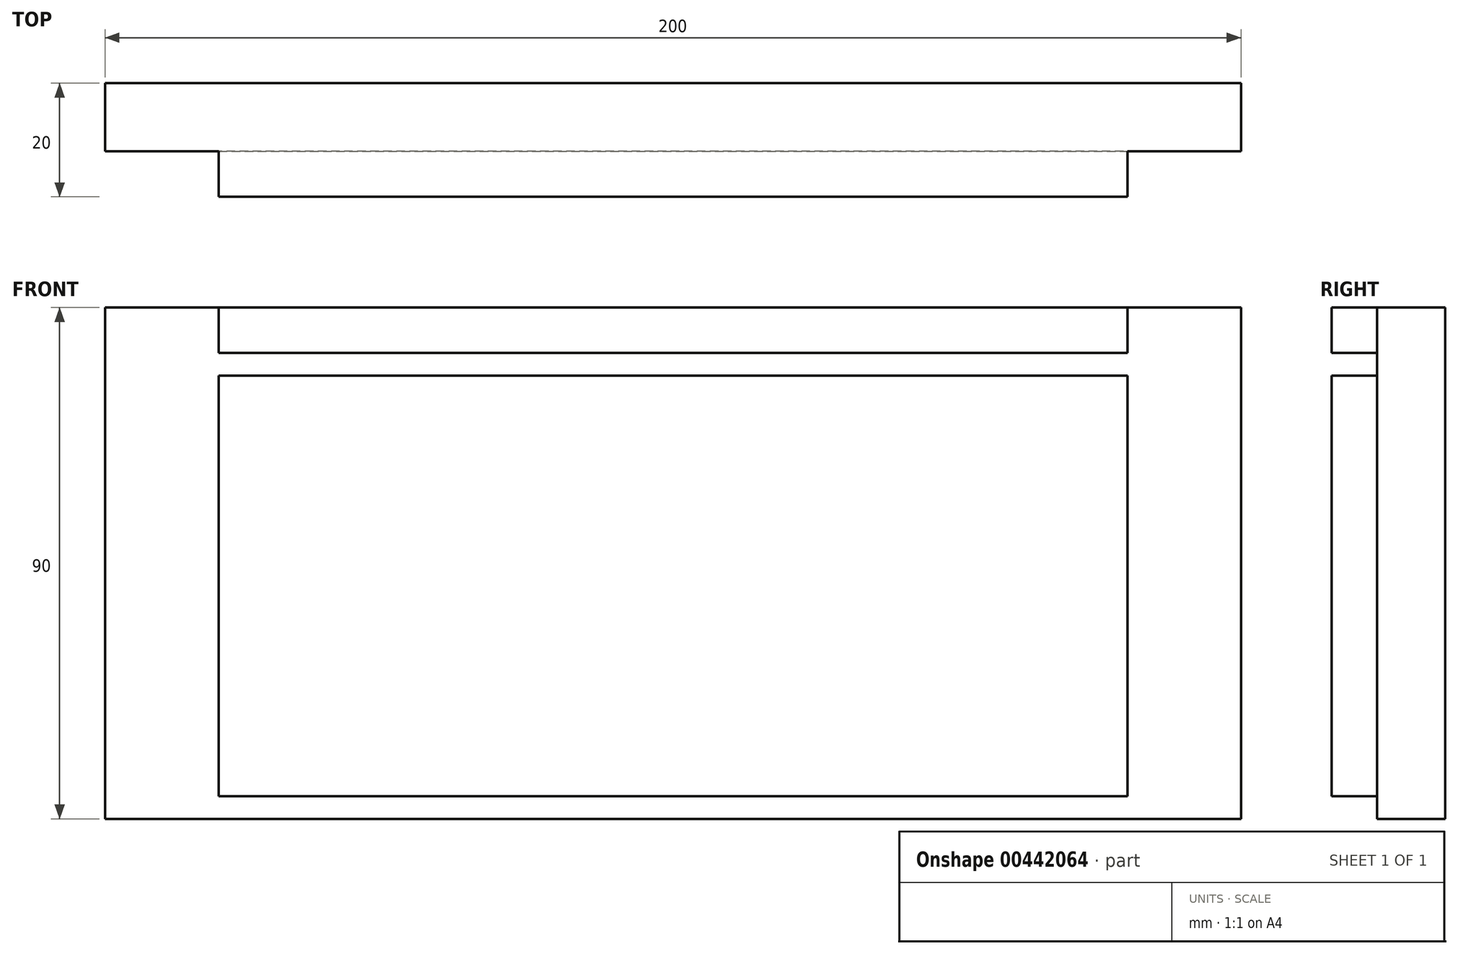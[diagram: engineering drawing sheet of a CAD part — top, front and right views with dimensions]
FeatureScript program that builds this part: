
annotation { "Feature Type Name" : "Feature", "Feature Type Description" : "" }
export const myFeature = defineFeature(function(context is Context, id is Id, definition is map)
    precondition{}
    {
        {
            var Q0;
            Q0=qCreatedBy(makeId("Front.planeOp"),FACE);
            var sketch = newSketch(context, id + "F0", { "sketchPlane" : qUnion([Q0])});
            skLineSegment(sketch, "E0.bottom", {"start": v(100, 45) * mm, "end": v(-100, 45) * mm});
            skLineSegment(sketch, "E0.top", {"start": v(100, -45) * mm, "end": v(-100, -45) * mm});
            skLineSegment(sketch, "E0.left", {"start": v(100, 45) * mm, "end": v(100, -45) * mm});
            skLineSegment(sketch, "E0.right", {"start": v(-100, 45) * mm, "end": v(-100, -45) * mm});
            skPoint(sketch, "E0.middle", {"position": v(0, 0) * mm});
            skLineSegment(sketch, "E1", {"start": v(-80, 45) * mm, "end": v(-80, -45) * mm});
            skLineSegment(sketch, "E2", {"start": v(80, 45) * mm, "end": v(80, -45) * mm});
            skLineSegment(sketch, "E3", {"start": v(-80, 37) * mm, "end": v(80, 37) * mm});
            skLineSegment(sketch, "E4", {"start": v(-80, 33) * mm, "end": v(80, 33) * mm});
            skLineSegment(sketch, "E5", {"start": v(-80, -41) * mm, "end": v(80, -41) * mm});
            skSolve(sketch);
        }
        {
            var Q0;
            {var subQ4=sQuery(id+"F0.wireOp",EDGE,"E0.right");Q0=makeQuery(id+"F0.imprint","IMPRINT",FACE,{"disambiguationData":[TD([[makeQuery(id+"F0.imprint","IMPRINT",EDGE,{"derivedFrom":subQ4}),1.0]])]});}
            var Q1;
            {var subQ0=sQuery(id+"F0.wireOp",EDGE,"E3");Q1=makeQuery(id+"F0.imprint","IMPRINT",FACE,{"disambiguationData":[TD([[makeQuery(id+"F0.imprint","IMPRINT",EDGE,{"derivedFrom":subQ0}),-1.0]])]});}
            var Q2;
            {var subQ5=sQuery(id+"F0.wireOp",EDGE,"E5");Q2=makeQuery(id+"F0.imprint","IMPRINT",FACE,{"disambiguationData":[TD([[makeQuery(id+"F0.imprint","IMPRINT",EDGE,{"derivedFrom":subQ5}),-1.0]])]});}
            var Q3;
            {var subQ4=sQuery(id+"F0.wireOp",EDGE,"E0.left");Q3=makeQuery(id+"F0.imprint","IMPRINT",FACE,{"disambiguationData":[TD([[makeQuery(id+"F0.imprint","IMPRINT",EDGE,{"derivedFrom":subQ4}),-1.0]])]});}
            extrude(context, id + "F1", {"entities" : qUnion([Q0, Q1, Q2, Q3]), "depth" : 12 * mm});
        }
        {
            var Q0;
            {var subQ5=sQuery(id+"F0.wireOp",EDGE,"E3");Q0=makeQuery(id+"F0.imprint","IMPRINT",FACE,{"disambiguationData":[TD([[makeQuery(id+"F0.imprint","IMPRINT",EDGE,{"derivedFrom":subQ5}),1.0]])]});}
            var Q1;
            {var subQ0=sQuery(id+"F0.wireOp",EDGE,"E4");Q1=makeQuery(id+"F0.imprint","IMPRINT",FACE,{"disambiguationData":[TD([[makeQuery(id+"F0.imprint","IMPRINT",EDGE,{"derivedFrom":subQ0}),-1.0]])]});}
            extrude(context, id + "F2", {"entities" : qUnion([Q0, Q1]), "operationType" : NewBodyOperationType.ADD, "depth" : 20 * mm});
        }
    });
